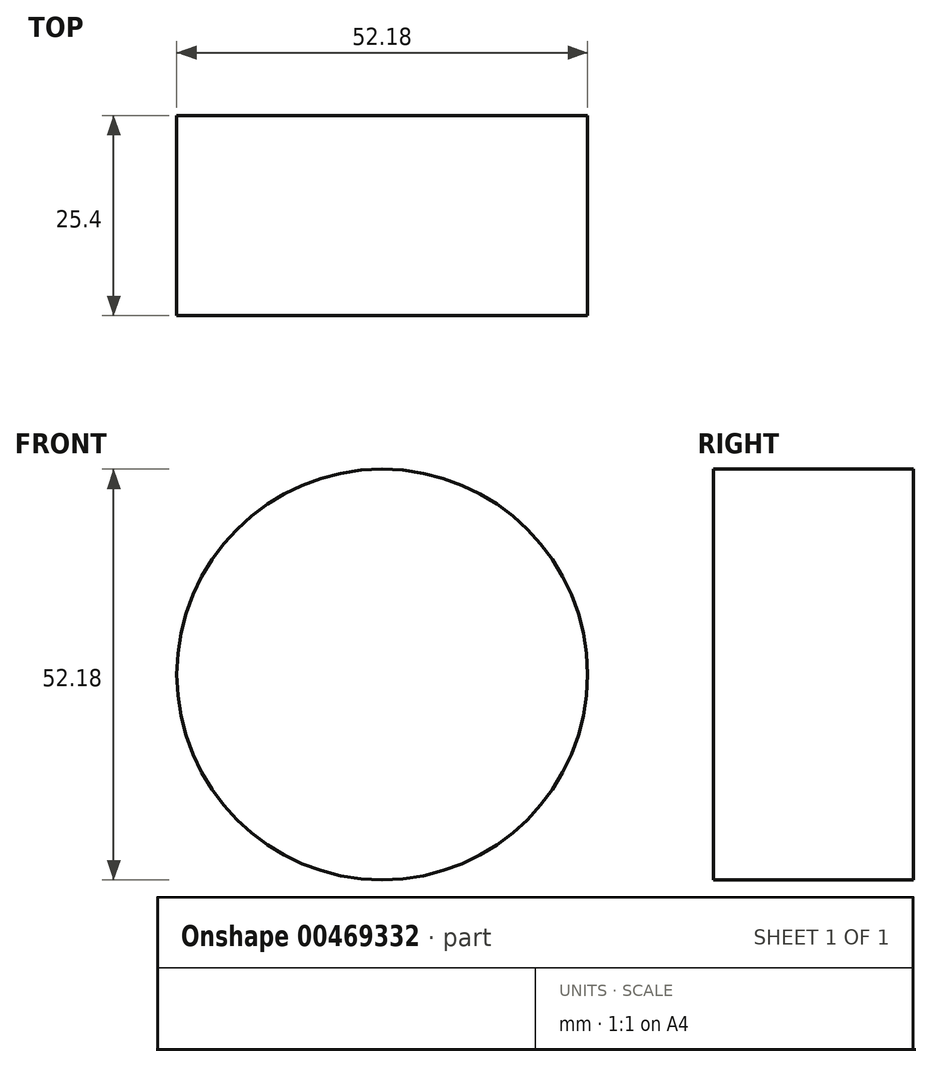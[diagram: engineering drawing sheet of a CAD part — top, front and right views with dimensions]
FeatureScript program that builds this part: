
annotation { "Feature Type Name" : "Feature", "Feature Type Description" : "" }
export const myFeature = defineFeature(function(context is Context, id is Id, definition is map)
    precondition{}
    {
        {
            var Q0;
            Q0=qCreatedBy(makeId("Front.planeOp"),FACE);
            var sketch = newSketch(context, id + "F0", { "sketchPlane" : qUnion([Q0])});
            skCircle(sketch, "E0", {"center": v(0, 0) * mm, "radius": 26.09 * mm});
            skSolve(sketch);
        }
        {
            var Q0;
            Q0=makeQuery(id+"F0.imprint","IMPRINT",FACE,{"disambiguationData":[TD([[makeQuery(id+"F0.imprint","IMPRINT",EDGE,{"derivedFrom":sQuery(id+"F0.wireOp",EDGE,"E0")}),1.0]])]});
            extrude(context, id + "F1", {"entities" : qUnion([Q0]), "depth" : 25.4 * mm});
        }
    });
